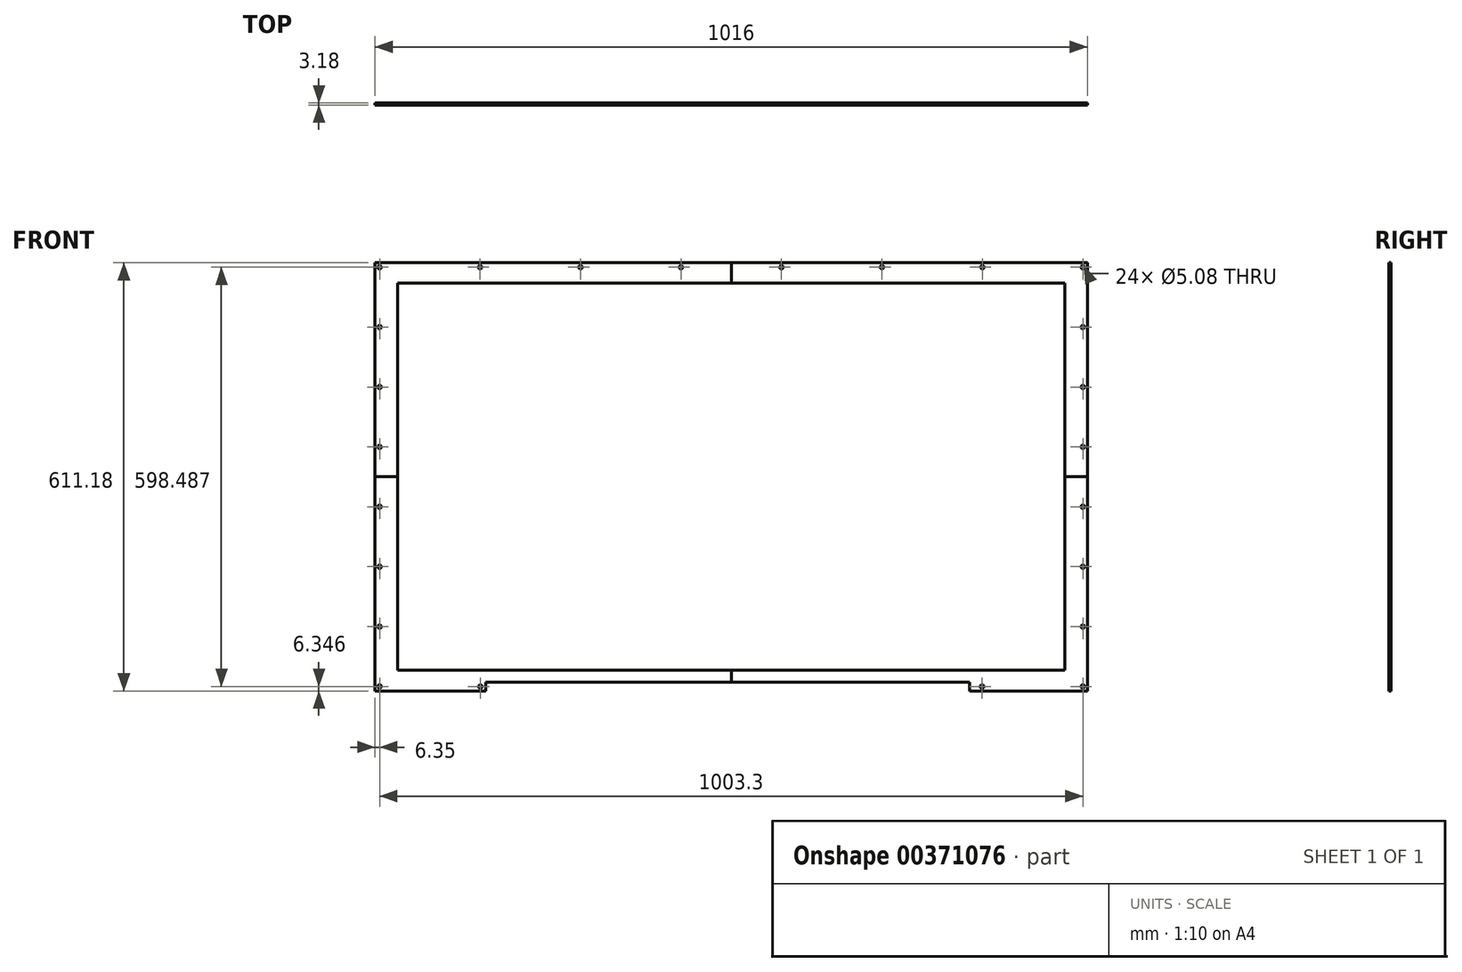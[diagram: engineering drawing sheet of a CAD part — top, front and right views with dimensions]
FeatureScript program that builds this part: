
annotation { "Feature Type Name" : "Feature", "Feature Type Description" : "" }
export const myFeature = defineFeature(function(context is Context, id is Id, definition is map)
    precondition{}
    {
        {
            var Q0;
            Q0=qCreatedBy(makeId("Front.planeOp"),FACE);
            var sketch = newSketch(context, id + "F0", { "sketchPlane" : qUnion([Q0])});
            skLineSegment(sketch, "E0.bottom", {"start": v(495.3, 292.9) * mm, "end": v(-495.3, 292.9) * mm});
            skLineSegment(sketch, "E0.top", {"start": v(495.3, -292.9) * mm, "end": v(-495.3, -292.9) * mm});
            skLineSegment(sketch, "E0.left", {"start": v(495.3, 292.9) * mm, "end": v(495.3, -292.9) * mm});
            skLineSegment(sketch, "E0.right", {"start": v(-495.3, 292.9) * mm, "end": v(-495.3, -292.9) * mm});
            skPoint(sketch, "E0.middle", {"position": v(0, 0) * mm});
            skLineSegment(sketch, "E1.0", {"start": v(-508, 305.6) * mm, "end": v(-508, -305.6) * mm});
            skLineSegment(sketch, "E1.1", {"start": v(508, 305.6) * mm, "end": v(-508, 305.6) * mm});
            skLineSegment(sketch, "E1.2", {"start": v(508, 305.6) * mm, "end": v(508, -305.6) * mm});
            skLineSegment(sketch, "E2", {"start": v(-508, 305.6) * mm, "end": v(-495.3, 292.9) * mm});
            skPoint(sketch, "E3.middle", {"position": v(-501.65, 299.24) * mm});
            skLineSegment(sketch, "E4", {"start": v(-350.3, -292.9) * mm, "end": v(-350.3, -305.6) * mm});
            skLineSegment(sketch, "E5", {"start": v(340.3, -292.9) * mm, "end": v(340.3, -305.6) * mm});
            skLineSegment(sketch, "E6.bottom", {"start": v(476, 276.23) * mm, "end": v(-476, 276.23) * mm});
            skLineSegment(sketch, "E6.top", {"start": v(476, -276.22) * mm, "end": v(-476, -276.23) * mm});
            skLineSegment(sketch, "E6.left", {"start": v(476, 276.23) * mm, "end": v(476, -276.23) * mm});
            skLineSegment(sketch, "E6.right", {"start": v(-476, 276.23) * mm, "end": v(-476, -276.23) * mm});
            skLineSegment(sketch, "E7", {"start": v(-495.3, -292.9) * mm, "end": v(-508, -305.6) * mm});
            skCircle(sketch, "E8", {"center": v(-501.65, 299.24) * mm, "radius": 2.54 * mm});
            skCircle(sketch, "E9", {"center": v(-358.32, 299.24) * mm, "radius": 2.54 * mm});
            skCircle(sketch, "E10", {"center": v(-215, 299.24) * mm, "radius": 2.54 * mm});
            skCircle(sketch, "E11", {"center": v(-71.66, 299.24) * mm, "radius": 2.54 * mm});
            skCircle(sketch, "E12", {"center": v(71.66, 299.24) * mm, "radius": 2.54 * mm});
            skCircle(sketch, "E13", {"center": v(215, 299.24) * mm, "radius": 2.54 * mm});
            skCircle(sketch, "E14", {"center": v(-501.65, 213.75) * mm, "radius": 2.54 * mm});
            skCircle(sketch, "E15", {"center": v(-501.65, 128.25) * mm, "radius": 2.54 * mm});
            skCircle(sketch, "E16", {"center": v(-501.65, 42.75) * mm, "radius": 2.54 * mm});
            skCircle(sketch, "E17", {"center": v(-501.65, -42.75) * mm, "radius": 2.54 * mm});
            skCircle(sketch, "E18", {"center": v(358.32, 299.24) * mm, "radius": 2.54 * mm});
            skCircle(sketch, "E19", {"center": v(501.65, 299.24) * mm, "radius": 2.54 * mm});
            skCircle(sketch, "E20", {"center": v(501.65, 213.75) * mm, "radius": 2.54 * mm});
            skCircle(sketch, "E21", {"center": v(501.65, 128.25) * mm, "radius": 2.54 * mm});
            skCircle(sketch, "E22", {"center": v(501.65, 42.75) * mm, "radius": 2.54 * mm});
            skCircle(sketch, "E23", {"center": v(501.65, -42.75) * mm, "radius": 2.54 * mm});
            skCircle(sketch, "E24", {"center": v(501.65, -128.25) * mm, "radius": 2.54 * mm});
            skCircle(sketch, "E25", {"center": v(501.65, -213.75) * mm, "radius": 2.54 * mm});
            skCircle(sketch, "E26", {"center": v(501.65, -299.24) * mm, "radius": 2.54 * mm});
            skCircle(sketch, "E27", {"center": v(357.84, -299.24) * mm, "radius": 2.54 * mm});
            skCircle(sketch, "E28", {"center": v(-357.84, -299.24) * mm, "radius": 2.54 * mm});
            skCircle(sketch, "E29", {"center": v(-501.65, -299.24) * mm, "radius": 2.54 * mm});
            skCircle(sketch, "E30", {"center": v(-501.65, -213.75) * mm, "radius": 2.54 * mm});
            skCircle(sketch, "E31", {"center": v(-501.65, -128.25) * mm, "radius": 2.54 * mm});
            skLineSegment(sketch, "E32", {"start": v(0, 276.23) * mm, "end": v(0, 305.6) * mm});
            skLineSegment(sketch, "E33", {"start": v(0, -276.22) * mm, "end": v(0, -292.9) * mm});
            skLineSegment(sketch, "E34", {"start": v(476, 0) * mm, "end": v(508, 0) * mm});
            skLineSegment(sketch, "E35", {"start": v(-508, -305.6) * mm, "end": v(-350.3, -305.6) * mm});
            skLineSegment(sketch, "E36", {"start": v(340.3, -305.6) * mm, "end": v(508, -305.6) * mm});
            skLineSegment(sketch, "E37", {"start": v(-476, 0) * mm, "end": v(-508, 0) * mm});
            skSolve(sketch);
        }
        {
            var Q0;
            {var subQ0=sQuery(id+"F0.wireOp",EDGE,"E6.right");var subQ1=sQuery(id+"F0.wireOp",EDGE,"E6.bottom");var subQ2=makeQuery(id+"F0.imprint","INTERSECT",VERTEX,{"derivedFrom":[subQ1,subQ0]});Q0=makeQuery(id+"F0.imprint","IMPRINT",FACE,{"disambiguationData":[TD([[makeQuery(id+"F0.imprint","IMPRINT",EDGE,{"disambiguationData":[TD([[subQ2,1.0]])],"derivedFrom":subQ1}),-1.0]])]});}
            var Q1;
            Q1=makeQuery(id+"F0.imprint","IMPRINT",FACE,{"disambiguationData":[TD([[makeQuery(id+"F0.imprint","IMPRINT",EDGE,{"derivedFrom":sQuery(id+"F0.wireOp",EDGE,"E14")}),-1.0]])]});
            var Q2;
            Q2=makeQuery(id+"F0.imprint","IMPRINT",FACE,{"disambiguationData":[TD([[makeQuery(id+"F0.imprint","IMPRINT",EDGE,{"derivedFrom":sQuery(id+"F0.wireOp",EDGE,"E9")}),-1.0]])]});
            extrude(context, id + "F1", {"entities" : qUnion([Q0, Q1, Q2]), "endBound" : BoundingType.SYMMETRIC, "depth" : 3.17 * mm});
        }
        {
            var Q0;
            {var subQ5=sQuery(id+"F0.wireOp",EDGE,"E0.left");var subQ6=sQuery(id+"F0.wireOp",EDGE,"E0.bottom");var subQ7=makeQuery(id+"F0.imprint","INTERSECT",VERTEX,{"derivedFrom":[subQ6,subQ5]});Q0=makeQuery(id+"F0.imprint","IMPRINT",FACE,{"disambiguationData":[TD([[makeQuery(id+"F0.imprint","IMPRINT",EDGE,{"disambiguationData":[TD([[subQ7,-1.0]])],"derivedFrom":subQ6}),1.0]])]});}
            var Q1;
            Q1=makeQuery(id+"F0.imprint","IMPRINT",FACE,{"disambiguationData":[TD([[makeQuery(id+"F0.imprint","IMPRINT",EDGE,{"derivedFrom":sQuery(id+"F0.wireOp",EDGE,"E12")}),-1.0]])]});
            extrude(context, id + "F2", {"entities" : qUnion([Q0, Q1]), "endBound" : BoundingType.SYMMETRIC, "depth" : 3.17 * mm});
        }
        {
            var Q0;
            {var subQ3=sQuery(id+"F0.wireOp",EDGE,"E33");Q0=makeQuery(id+"F0.imprint","IMPRINT",FACE,{"disambiguationData":[TD([[makeQuery(id+"F0.imprint","IMPRINT",EDGE,{"derivedFrom":subQ3}),1.0]])]});}
            var Q1;
            {var subQ3=sQuery(id+"F0.wireOp",EDGE,"E5");Q1=makeQuery(id+"F0.imprint","IMPRINT",FACE,{"disambiguationData":[TD([[makeQuery(id+"F0.imprint","IMPRINT",EDGE,{"derivedFrom":subQ3}),1.0]])]});}
            extrude(context, id + "F3", {"entities" : qUnion([Q0, Q1]), "endBound" : BoundingType.SYMMETRIC, "depth" : 3.17 * mm});
        }
        {
            var Q0;
            {var subQ4=sQuery(id+"F0.wireOp",EDGE,"E33");Q0=makeQuery(id+"F0.imprint","IMPRINT",FACE,{"disambiguationData":[TD([[makeQuery(id+"F0.imprint","IMPRINT",EDGE,{"derivedFrom":subQ4}),-1.0]])]});}
            var Q1;
            {var subQ7=sQuery(id+"F0.wireOp",EDGE,"E4");Q1=makeQuery(id+"F0.imprint","IMPRINT",FACE,{"disambiguationData":[TD([[makeQuery(id+"F0.imprint","IMPRINT",EDGE,{"derivedFrom":subQ7}),-1.0]])]});}
            var Q2;
            Q2=makeQuery(id+"F0.imprint","IMPRINT",FACE,{"disambiguationData":[TD([[makeQuery(id+"F0.imprint","IMPRINT",EDGE,{"derivedFrom":sQuery(id+"F0.wireOp",EDGE,"E17")}),-1.0]])]});
            extrude(context, id + "F4", {"entities" : qUnion([Q0, Q1, Q2]), "endBound" : BoundingType.SYMMETRIC, "depth" : 3.17 * mm});
        }
    });
